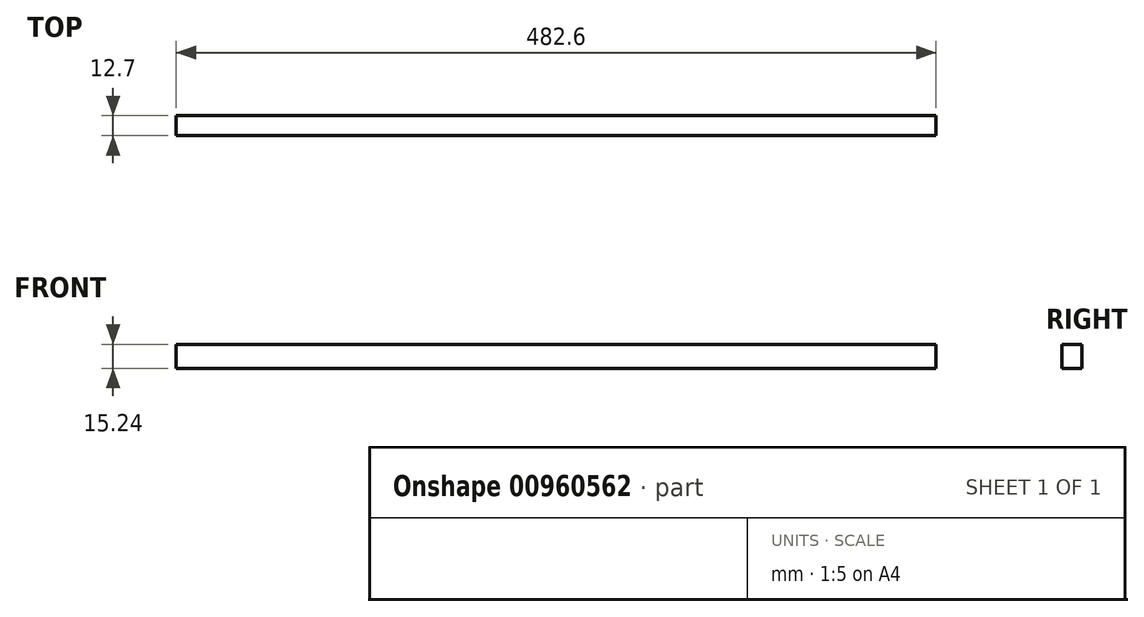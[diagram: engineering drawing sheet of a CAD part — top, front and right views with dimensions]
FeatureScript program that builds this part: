
annotation { "Feature Type Name" : "Feature", "Feature Type Description" : "" }
export const myFeature = defineFeature(function(context is Context, id is Id, definition is map)
    precondition{}
    {
        {
            var Q0;
            Q0=qCreatedBy(makeId("Front.planeOp"),FACE);
            var sketch = newSketch(context, id + "F0", { "sketchPlane" : qUnion([Q0])});
            skLineSegment(sketch, "E0.bottom", {"start": v(-227.59, -2.9) * mm, "end": v(255.01, -2.9) * mm});
            skLineSegment(sketch, "E0.top", {"start": v(-227.59, -18.14) * mm, "end": v(255.01, -18.14) * mm});
            skLineSegment(sketch, "E0.left", {"start": v(-227.59, -2.9) * mm, "end": v(-227.59, -18.14) * mm});
            skLineSegment(sketch, "E0.right", {"start": v(255.01, -2.9) * mm, "end": v(255.01, -18.14) * mm});
            skPoint(sketch, "E0.middle", {"position": v(13.71, -10.52) * mm});
            skSolve(sketch);
        }
        {
            var Q0;
            Q0 = qSketchRegion(id + "F0", true);
            extrude(context, id + "F1", {"entities" : qUnion([Q0]), "depth" : 12.7 * mm, "offsetDistance" : 25.4 * mm});
        }
    });
